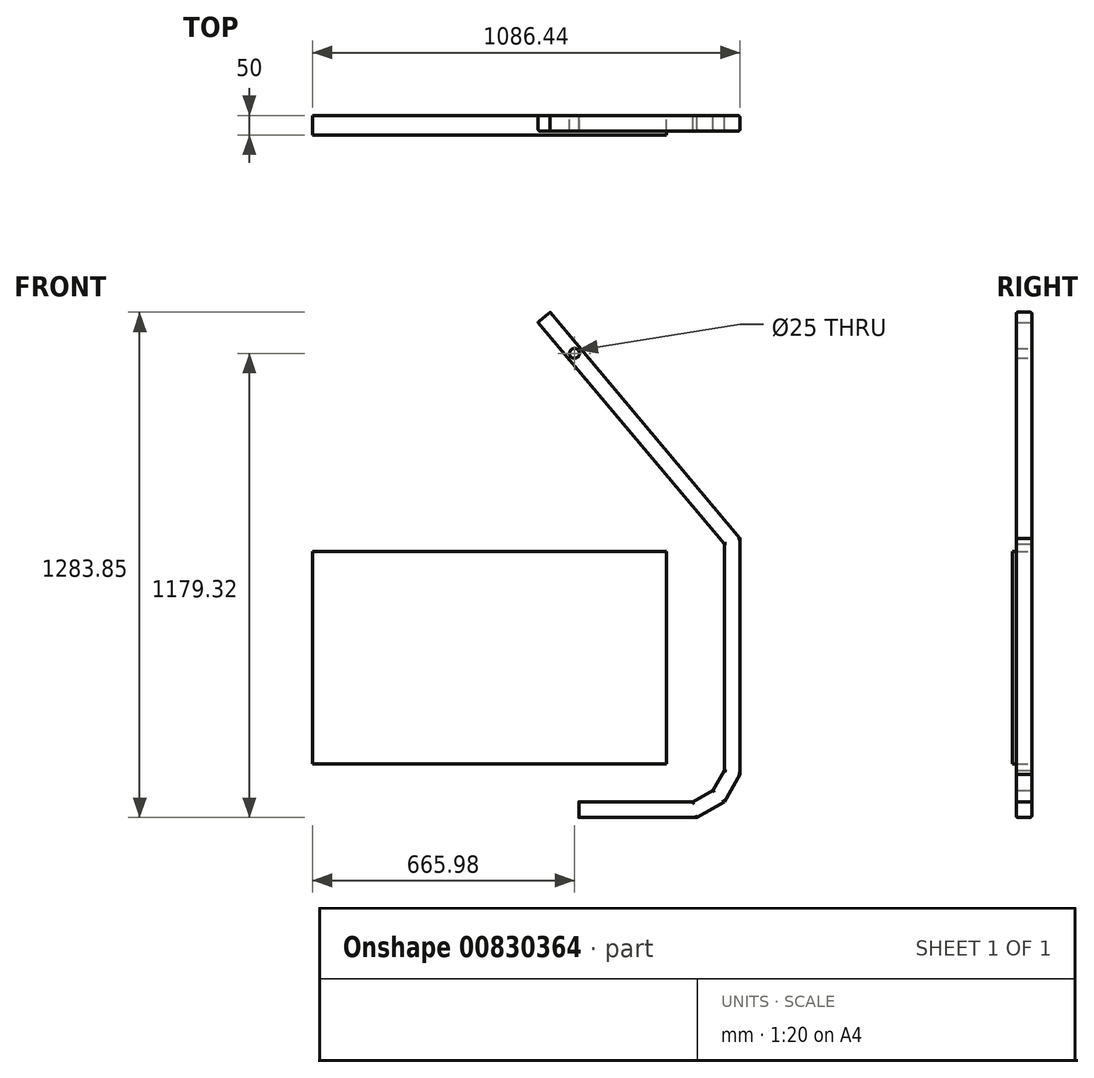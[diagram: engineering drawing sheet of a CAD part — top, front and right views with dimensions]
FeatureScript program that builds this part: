
annotation { "Feature Type Name" : "Feature", "Feature Type Description" : "" }
export const myFeature = defineFeature(function(context is Context, id is Id, definition is map)
    precondition{}
    {
        {
            var Q0;
            Q0=qCreatedBy(makeId("Front.planeOp"),FACE);
            var sketch = newSketch(context, id + "F0", { "sketchPlane" : qUnion([Q0])});
            skLineSegment(sketch, "E0.bottom", {"start": v(-317.16, 26.23) * mm, "end": v(-27.85, 26.23) * mm});
            skLineSegment(sketch, "E0.top", {"start": v(-317.16, -13.77) * mm, "end": v(-17.16, -13.77) * mm});
            skLineSegment(sketch, "E0.left", {"start": v(-317.16, 26.23) * mm, "end": v(-317.16, -13.77) * mm});
            skLineSegment(sketch, "E1", {"start": v(-17.16, -13.77) * mm, "end": v(52.12, 26.23) * mm});
            skLineSegment(sketch, "E2", {"start": v(-17.16, -13.77) * mm, "end": v(-27.85, 26.23) * mm});
            skLineSegment(sketch, "E3", {"start": v(-27.85, 26.23) * mm, "end": v(22.86, 55.52) * mm});
            skLineSegment(sketch, "E4", {"start": v(52.12, 26.23) * mm, "end": v(22.86, 55.52) * mm});
            skLineSegment(sketch, "E5", {"start": v(52.12, 26.23) * mm, "end": v(92.13, 95.51) * mm});
            skLineSegment(sketch, "E6", {"start": v(92.13, 95.51) * mm, "end": v(92.13, 695.51) * mm});
            skLineSegment(sketch, "E7", {"start": v(92.13, 95.51) * mm, "end": v(52.14, 106.23) * mm});
            skLineSegment(sketch, "E8", {"start": v(52.14, 106.23) * mm, "end": v(22.86, 55.52) * mm});
            skLineSegment(sketch, "E9", {"start": v(52.14, 106.23) * mm, "end": v(52.14, 680.98) * mm});
            skLineSegment(sketch, "E10", {"start": v(52.14, 680.98) * mm, "end": v(92.13, 695.51) * mm});
            skLineSegment(sketch, "E11", {"start": v(92.13, 695.51) * mm, "end": v(-389.93, 1270.08) * mm});
            skPoint(sketch, "E12", {"position": v(-317.16, 1183.34) * mm});
            skLineSegment(sketch, "E13", {"start": v(-389.93, 1270.08) * mm, "end": v(-420.57, 1244.37) * mm});
            skLineSegment(sketch, "E14", {"start": v(-420.57, 1244.37) * mm, "end": v(52.14, 680.98) * mm});
            skPoint(sketch, "E15", {"position": v(-328.33, 1165.55) * mm});
            skCircle(sketch, "E16", {"center": v(-328.33, 1165.55) * mm, "radius": 12.5 * mm});
            skSolve(sketch);
        }
        {
            var Q0;
            Q0 = qSketchRegion(id + "F0", true);
            extrude(context, id + "F1", {"entities" : qUnion([Q0]), "depth" : 40 * mm, "offsetDistance" : 25.4 * mm});
        }
        {
            var Q0;
            Q0=makeQuery(id+"F1.opExtrude","CAP_EDGE",EDGE,{"disambiguationData":[OSD([sQuery(id+"F0.wireOp",EDGE,"E11")])],"isStart":false});
            var Q1;
            Q1=makeQuery(id+"F1.opExtrude","CAP_EDGE",EDGE,{"disambiguationData":[OSD([sQuery(id+"F0.wireOp",EDGE,"E14")])],"isStart":true});
            var Q2;
            Q2=makeQuery(id+"F1.opExtrude","CAP_EDGE",EDGE,{"disambiguationData":[OSD([sQuery(id+"F0.wireOp",EDGE,"E14")])],"isStart":false});
            var Q3;
            Q3=makeQuery(id+"F1.opExtrude","CAP_EDGE",EDGE,{"disambiguationData":[OSD([sQuery(id+"F0.wireOp",EDGE,"E11")])],"isStart":true});
            var Q4;
            Q4=makeQuery(id+"F1.opExtrude","CAP_EDGE",EDGE,{"disambiguationData":[OSD([sQuery(id+"F0.wireOp",EDGE,"E9")])],"isStart":true});
            var Q5;
            Q5=makeQuery(id+"F1.opExtrude","CAP_EDGE",EDGE,{"disambiguationData":[OSD([sQuery(id+"F0.wireOp",EDGE,"E9")])],"isStart":false});
            var Q6;
            Q6=makeQuery(id+"F1.opExtrude","CAP_EDGE",EDGE,{"disambiguationData":[OSD([sQuery(id+"F0.wireOp",EDGE,"E6")])],"isStart":true});
            var Q7;
            Q7=makeQuery(id+"F1.opExtrude","CAP_EDGE",EDGE,{"disambiguationData":[OSD([sQuery(id+"F0.wireOp",EDGE,"E0.bottom")])],"isStart":false});
            var Q8;
            Q8=makeQuery(id+"F1.opExtrude","CAP_EDGE",EDGE,{"disambiguationData":[OSD([sQuery(id+"F0.wireOp",EDGE,"E8")])],"isStart":false});
            var Q9;
            Q9=makeQuery(id+"F1.opExtrude","CAP_EDGE",EDGE,{"disambiguationData":[OSD([sQuery(id+"F0.wireOp",EDGE,"E3")])],"isStart":false});
            var Q10;
            Q10=makeQuery(id+"F1.opExtrude","CAP_EDGE",EDGE,{"disambiguationData":[OSD([sQuery(id+"F0.wireOp",EDGE,"E8")])],"isStart":true});
            var Q11;
            Q11=makeQuery(id+"F1.opExtrude","CAP_EDGE",EDGE,{"disambiguationData":[OSD([sQuery(id+"F0.wireOp",EDGE,"E3")])],"isStart":true});
            var Q12;
            Q12=makeQuery(id+"F1.opExtrude","CAP_EDGE",EDGE,{"disambiguationData":[OSD([sQuery(id+"F0.wireOp",EDGE,"E0.bottom")])],"isStart":true});
            var Q13;
            Q13=makeQuery(id+"F1.opExtrude","CAP_EDGE",EDGE,{"disambiguationData":[OSD([sQuery(id+"F0.wireOp",EDGE,"E0.top")])],"isStart":true});
            var Q14;
            Q14=makeQuery(id+"F1.opExtrude","CAP_EDGE",EDGE,{"disambiguationData":[OSD([sQuery(id+"F0.wireOp",EDGE,"E1")])],"isStart":true});
            var Q15;
            Q15=makeQuery(id+"F1.opExtrude","CAP_EDGE",EDGE,{"disambiguationData":[OSD([sQuery(id+"F0.wireOp",EDGE,"E5")])],"isStart":true});
            var Q16;
            Q16=makeQuery(id+"F1.opExtrude","CAP_EDGE",EDGE,{"disambiguationData":[OSD([sQuery(id+"F0.wireOp",EDGE,"E0.top")])],"isStart":false});
            var Q17;
            Q17=makeQuery(id+"F1.opExtrude","CAP_EDGE",EDGE,{"disambiguationData":[OSD([sQuery(id+"F0.wireOp",EDGE,"E1")])],"isStart":false});
            var Q18;
            Q18=makeQuery(id+"F1.opExtrude","CAP_EDGE",EDGE,{"disambiguationData":[OSD([sQuery(id+"F0.wireOp",EDGE,"E5")])],"isStart":false});
            var Q19;
            Q19=makeQuery(id+"F1.opExtrude","CAP_EDGE",EDGE,{"disambiguationData":[OSD([sQuery(id+"F0.wireOp",EDGE,"E6")])],"isStart":false});
            fillet(context, id + "F2", {"entities" : qUnion([Q0, Q1, Q2, Q3, Q4, Q5, Q6, Q7, Q8, Q9, Q10, Q11, Q12, Q13, Q14, Q15, Q16, Q17, Q18, Q19]), "radius" : 5 * mm, "tangentPropagation" : true, "allowEdgeOverflow" : false});
        }
        {
            var Q0;
            Q0=qCreatedBy(makeId("Front.planeOp"),FACE);
            var sketch = newSketch(context, id + "F3", { "sketchPlane" : qUnion([Q0])});
            skLineSegment(sketch, "E17", {"start": v(-94.31, 122.78) * mm, "end": v(-994.31, 122.78) * mm});
            skLineSegment(sketch, "E18", {"start": v(-516.63, 122.78) * mm, "end": v(-516.63, -620.07) * mm});
            skLineSegment(sketch, "E19", {"start": v(-94.31, 122.78) * mm, "end": v(-94.31, 662.78) * mm});
            skLineSegment(sketch, "E20", {"start": v(-994.31, 122.78) * mm, "end": v(-994.31, 662.78) * mm});
            skLineSegment(sketch, "E21", {"start": v(-994.31, 662.78) * mm, "end": v(-94.31, 662.78) * mm});
            skSolve(sketch);
        }
        {
            var Q0;
            Q0 = qSketchRegion(id + "F3", true);
            var Q1;
            {var subQ1=sQuery(id+"F3.wireOp",EDGE,"E19");Q1=makeQuery(id+"F3.imprint","IMPRINT",FACE,{"disambiguationData":[TD([[makeQuery(id+"F3.imprint","IMPRINT",EDGE,{"derivedFrom":subQ1}),1.0]])]});}
            extrude(context, id + "F4", {"entities" : qUnion([Q0, Q1]), "depth" : 50 * mm, "offsetDistance" : 25.4 * mm});
        }
    });
